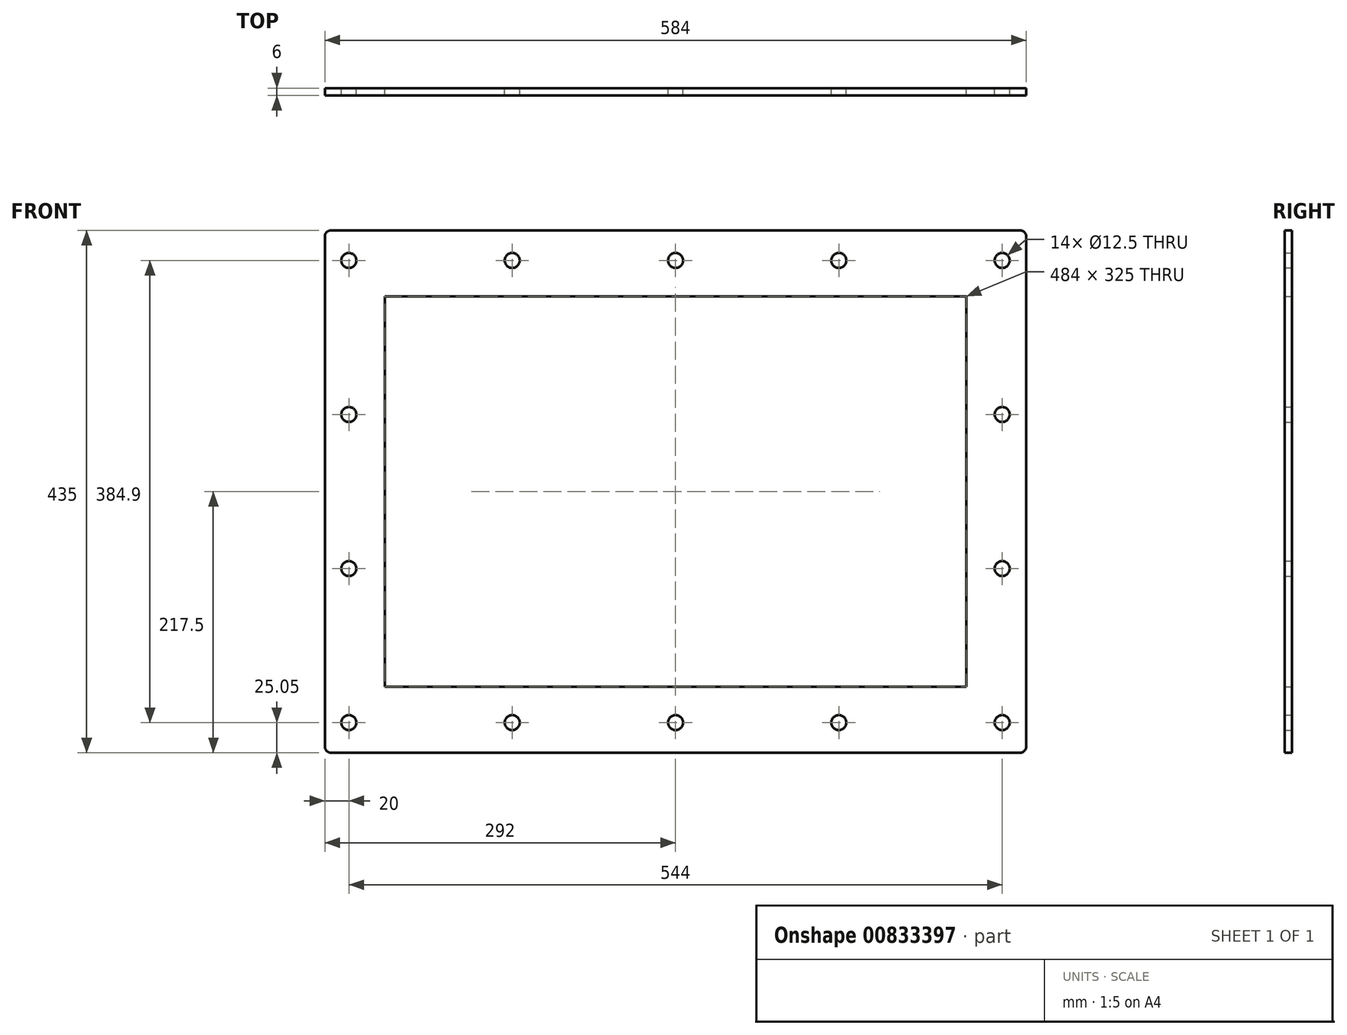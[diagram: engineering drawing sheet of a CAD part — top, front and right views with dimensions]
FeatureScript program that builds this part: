
annotation { "Feature Type Name" : "Feature", "Feature Type Description" : "" }
export const myFeature = defineFeature(function(context is Context, id is Id, definition is map)
    precondition{}
    {
        {
            var Q0;
            Q0=qCreatedBy(makeId("Front.planeOp"),FACE);
            var sketch = newSketch(context, id + "F0", { "sketchPlane" : qUnion([Q0])});
            skLineSegment(sketch, "E0.bottom", {"start": v(242, -162.5) * mm, "end": v(-242, -162.5) * mm});
            skLineSegment(sketch, "E0.top", {"start": v(242, 162.5) * mm, "end": v(-242, 162.5) * mm});
            skLineSegment(sketch, "E0.left", {"start": v(242, -162.5) * mm, "end": v(242, 162.5) * mm});
            skLineSegment(sketch, "E0.right", {"start": v(-242, -162.5) * mm, "end": v(-242, 162.5) * mm});
            skPoint(sketch, "E0.middle", {"position": v(0, 0) * mm});
            skLineSegment(sketch, "E1.bottom", {"start": v(287, -217.5) * mm, "end": v(-287, -217.5) * mm});
            skLineSegment(sketch, "E1.top", {"start": v(287, 217.5) * mm, "end": v(-287, 217.5) * mm});
            skLineSegment(sketch, "E1.left", {"start": v(292, -212.5) * mm, "end": v(292, 212.5) * mm});
            skLineSegment(sketch, "E1.right", {"start": v(-292, -212.5) * mm, "end": v(-292, 212.5) * mm});
            skPoint(sketch, "E2.visualSharp", {"position": v(-242, 162.5) * mm});
            skPoint(sketch, "E3.visualSharp", {"position": v(-292, 217.5) * mm});
            skArc(sketch, "E3.filletArc", {"start": v(-287, 217.5) * mm, "mid": v(-290.54, 216.04) * mm, "end": v(-292, 212.5) * mm});
            skPoint(sketch, "E4.visualSharp", {"position": v(-292, -217.5) * mm});
            skArc(sketch, "E4.filletArc", {"start": v(-292, -212.5) * mm, "mid": v(-290.54, -216.04) * mm, "end": v(-287, -217.5) * mm});
            skPoint(sketch, "E5.visualSharp", {"position": v(-242, -162.5) * mm});
            skPoint(sketch, "E6.visualSharp", {"position": v(242, -162.5) * mm});
            skPoint(sketch, "E7.visualSharp", {"position": v(292, -217.5) * mm});
            skArc(sketch, "E7.filletArc", {"start": v(287, -217.5) * mm, "mid": v(290.54, -216.04) * mm, "end": v(292, -212.5) * mm});
            skPoint(sketch, "E8.visualSharp", {"position": v(292, 217.5) * mm});
            skArc(sketch, "E8.filletArc", {"start": v(292, 212.5) * mm, "mid": v(290.54, 216.04) * mm, "end": v(287, 217.5) * mm});
            skPoint(sketch, "E9.visualSharp", {"position": v(242, 162.5) * mm});
            skSolve(sketch);
        }
        {
            var Q0;
            Q0=makeQuery(id+"F0.imprint","IMPRINT",FACE,{"disambiguationData":[TD([[makeQuery(id+"F0.imprint","IMPRINT",EDGE,{"derivedFrom":sQuery(id+"F0.wireOp",EDGE,"E0.bottom")}),1.0]])]});
            extrude(context, id + "F1", {"entities" : qUnion([Q0]), "depth" : 6 * mm, "offsetDistance" : 25 * mm});
        }
        {
            var Q0;
            Q0=qCreatedBy(makeId("Front.planeOp"),FACE);
            var sketch = newSketch(context, id + "F2", { "sketchPlane" : qUnion([Q0])});
            skLineSegment(sketch, "E10", {"start": v(0, 0) * mm, "end": v(417.5, 0) * mm, "construction": true});
            skLineSegment(sketch, "E11", {"start": v(0, 0) * mm, "end": v(0, 311.58) * mm, "construction": true});
            skPoint(sketch, "E12", {"position": v(-272, -192.45) * mm});
            skPoint(sketch, "E13.0.1.0", {"position": v(-272, -64.15) * mm});
            skPoint(sketch, "E13.0.2.0", {"position": v(-272, 64.15) * mm});
            skPoint(sketch, "E13.0.3.0", {"position": v(-272, 192.45) * mm});
            skPoint(sketch, "E13.1.0.0", {"position": v(-136, -192.45) * mm});
            skPoint(sketch, "E13.1.1.0", {"position": v(-136, -64.15) * mm});
            skPoint(sketch, "E13.1.2.0", {"position": v(-136, 64.15) * mm});
            skPoint(sketch, "E13.1.3.0", {"position": v(-136, 192.45) * mm});
            skPoint(sketch, "E13.2.0.0", {"position": v(0, -192.45) * mm});
            skPoint(sketch, "E13.2.1.0", {"position": v(0, -64.15) * mm});
            skPoint(sketch, "E13.2.2.0", {"position": v(0, 64.15) * mm});
            skPoint(sketch, "E13.2.3.0", {"position": v(0, 192.45) * mm});
            skPoint(sketch, "E13.3.0.0", {"position": v(136, -192.45) * mm});
            skPoint(sketch, "E13.3.1.0", {"position": v(136, -64.15) * mm});
            skPoint(sketch, "E13.3.2.0", {"position": v(136, 64.15) * mm});
            skPoint(sketch, "E13.3.3.0", {"position": v(136, 192.45) * mm});
            skPoint(sketch, "E13.4.0.0", {"position": v(272, -192.45) * mm});
            skPoint(sketch, "E13.4.1.0", {"position": v(272, -64.15) * mm});
            skPoint(sketch, "E13.4.2.0", {"position": v(272, 64.15) * mm});
            skPoint(sketch, "E13.4.3.0", {"position": v(272, 192.45) * mm});
            skLineSegment(sketch, "E13.direction1", {"start": v(-272, -192.45) * mm, "end": v(-136, -192.45) * mm, "construction": true});
            skLineSegment(sketch, "E13.direction2", {"start": v(-272, -192.45) * mm, "end": v(-272, -64.15) * mm, "construction": true});
            skSolve(sketch);
        }
        {
            var Q0;
            Q0=sQuery(id+"F2.wireOp",VERTEX,"E13.0.3.0");
            var Q1;
            Q1=sQuery(id+"F2.wireOp",VERTEX,"E13.0.2.0");
            var Q2;
            Q2=sQuery(id+"F2.wireOp",VERTEX,"E13.0.1.0");
            var Q3;
            Q3=sQuery(id+"F2.wireOp",VERTEX,"E12");
            var Q4;
            Q4=sQuery(id+"F2.wireOp",VERTEX,"E13.1.0.0");
            var Q5;
            Q5=sQuery(id+"F2.wireOp",VERTEX,"E13.2.0.0");
            var Q6;
            Q6=sQuery(id+"F2.wireOp",VERTEX,"E13.4.0.0");
            var Q7;
            Q7=sQuery(id+"F2.wireOp",VERTEX,"E13.3.0.0");
            var Q8;
            Q8=sQuery(id+"F2.wireOp",VERTEX,"E13.4.2.0");
            var Q9;
            Q9=sQuery(id+"F2.wireOp",VERTEX,"E13.4.1.0");
            var Q10;
            Q10=sQuery(id+"F2.wireOp",VERTEX,"E13.4.3.0");
            var Q11;
            Q11=sQuery(id+"F2.wireOp",VERTEX,"E13.1.3.0");
            var Q12;
            Q12=sQuery(id+"F2.wireOp",VERTEX,"E13.3.3.0");
            var Q13;
            Q13=sQuery(id+"F2.wireOp",VERTEX,"E13.2.3.0");
            var Q14;
            Q14=makeQuery(id+"F1.opExtrude","SWEPT_BODY",BODY,{"disambiguationData":[OSD([sQuery(id+"F0.wireOp",EDGE,"E0.bottom"),sQuery(id+"F0.wireOp",EDGE,"E0.top"),sQuery(id+"F0.wireOp",EDGE,"E0.left"),sQuery(id+"F0.wireOp",EDGE,"E0.right"),sQuery(id+"F0.wireOp",EDGE,"E1.bottom"),sQuery(id+"F0.wireOp",EDGE,"E1.top"),sQuery(id+"F0.wireOp",EDGE,"E1.left"),sQuery(id+"F0.wireOp",EDGE,"E1.right"),sQuery(id+"F0.wireOp",EDGE,"E2.filletArc"),sQuery(id+"F0.wireOp",EDGE,"E3.filletArc"),sQuery(id+"F0.wireOp",EDGE,"E4.filletArc"),sQuery(id+"F0.wireOp",EDGE,"E5.filletArc"),sQuery(id+"F0.wireOp",EDGE,"E6.filletArc"),sQuery(id+"F0.wireOp",EDGE,"E7.filletArc"),sQuery(id+"F0.wireOp",EDGE,"E8.filletArc"),sQuery(id+"F0.wireOp",EDGE,"E9.filletArc")])]});
            hole(context, id + "F3", {"style" : HoleStyle.SIMPLE, "endStyle" : HoleEndStyle.THROUGH, "oppositeDirection" : true, "standardTappedOrClearance" : lookupTablePath({ "standard" : "ISO", "size" : "12.5", "type" : "Drilled" }), "standardBlindInLast" : lookupTablePath({ "standard" : "ISO", "size" : "12.5", "type" : "Drilled" }), "holeDiameter" : 12.5 * mm, "majorDiameter" : 5 * mm, "isTappedThrough" : true, "tappedDepth" : 12 * mm, "tapClearance" : 3, "startFromSketch" : true, "locations" : qUnion([Q0, Q1, Q2, Q3, Q4, Q5, Q6, Q7, Q8, Q9, Q10, Q11, Q12, Q13]), "scope" : qUnion([Q14])});
        }
    });
